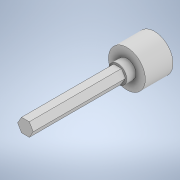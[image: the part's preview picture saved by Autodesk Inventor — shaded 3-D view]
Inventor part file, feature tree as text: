
AUTODESK INVENTOR PART (.ipt)
format: ipt  version: 2021.2 (Build 252289000, 289)  size: 136,192 bytes
history: native  units: in
note: dims shown in document units (in); Inventor stores cm internally (conversion verified against a paired STEP export)
features: extrude x3, sketch x3, other x2
ambient origin geometry x8: Origin, YZ Plane, XZ Plane, XY Plane, X Axis, Y Axis, Z Axis, Center Point
bodies: Body1 (feature_tree)
feature tree (8):
  extrude  "Extrusion2"  Depth=3.5in TaperAngle=0.0deg
  extrude  "Extrusion4"  Depth=1.0in
  other  "Reduce Hex Shaft"
  extrude  "Extrusion5"  Depth=0.25in
  other  "Reduce Base Bushing"
  sketch  "Sketch1"  dims[d0=0.375in d4=3.5in d5=0.0in]
  sketch  "Sketch4"  dims[d6=0.001in d10=1.0in]
  sketch  "Sketch5"  dims[d11=0.75in d12=0.0in d13=0.005in d14=0.005in d15=0.5in d16=0.25in d17=0.0in d20=0.005in d21=0.005in]
